# Revit family: Detail-HST Top Hat-Steel & Tube-HST-Section
name_source: partatom
category: Detail Items
revit_build: Autodesk Revit 2017 (Build: 20170118_1100(x64)
units: mm (PartAtom-declared; Revit-internal decimal feet)

## family parameters
OmniClass Number = 23.35.20.14.14
OmniClass Title = Roof Battens
Rotate with component = No
Section Shape = Not Defined
Shared = No

## types (8) — shared parameters
Assembly Code = B1020230
CBICode = 3411
CBIDescription = Structural steelwork
Coil Performance = Gauge 0.75-1.15mm; G500(MPa); 275g/m² (Zinc)
Description = Steel & Tube HST Tophat sections are an economical, lightweight, versatile and easy to use product for roof purlins, wall girts and floor joists.
Design Instruction = All the design information should be cross referenced with the current Steel & Tube Tophat Design Capacity Tables.
Design Standard = Steel & Tube’s HST Tophat profiles are designed in accordance with AS/NZS 4600:2005
Manufacturer = Steel & Tube
ManufacturerName = Steel & Tube
ManufacturerURL = http://www.steelandtube.co.nz
Material Standard = Steel & Tube’s HST Tophat profiles are manufactured from materials conforming to AS1397:2011
ModifiedIssue_ANZRS = 20160526 $
Profile74 = No
Profile75 = No
Profile76 = No
SpecificationDescription = Steel & Tube Purlins & Girts
SpecificationReference = 3411ST
URL = http://www.steelandtube.co.nz
Uniclass2015Code = Pr_20_76_51_21
Uniclass2015Title = Cold-formed galvanized steel sections
Uniclass2015Version = 2015

## per-type parameters (varying)
| type | Height_ANZRS | Profile | Profile70 | Profile71 | Profile72 | Profile73 | Width_ANZRS |
| 60 HST Tophat 0.75 BMT | 60 mm  [stored 0.19685 ft] | 0 | Yes | No | No | No | 108 mm  [stored 0.354331 ft] |
| 60 HST Tophat 0.95 BMT | 60 mm  [stored 0.19685 ft] | 0 | Yes | No | No | No | 108 mm  [stored 0.354331 ft] |
| 100 HST Tophat 0.75 BMT | 100 mm  [stored 0.328084 ft] | 1 | No | Yes | No | No | 163 mm  [stored 0.534777 ft] |
| 100 HST Tophat 0.95 BMT | 100 mm  [stored 0.328084 ft] | 1 | No | Yes | No | No | 163 mm  [stored 0.534777 ft] |
| 120 HST Tophat 0.75 BMT | 120 mm  [stored 0.393701 ft] | 2 | No | No | Yes | No | 170 mm  [stored 0.557743 ft] |
| 120 HST Tophat 0.95 BMT | 120 mm  [stored 0.393701 ft] | 2 | No | No | Yes | No | 170 mm  [stored 0.557743 ft] |
| 150 HST Tophat 0.95 BMT | 150 mm | 3 | No | No | No | Yes | 183 mm |
| 150 HST Tophat 1.15 BMT | 150 mm | 3 | No | No | No | Yes | 183 mm |

note: column(s) folded — value = type name in every type: Model

note: [stored X ft] marks values corroborated as IEEE doubles in the binary element streams (Revit-internal decimal feet)
